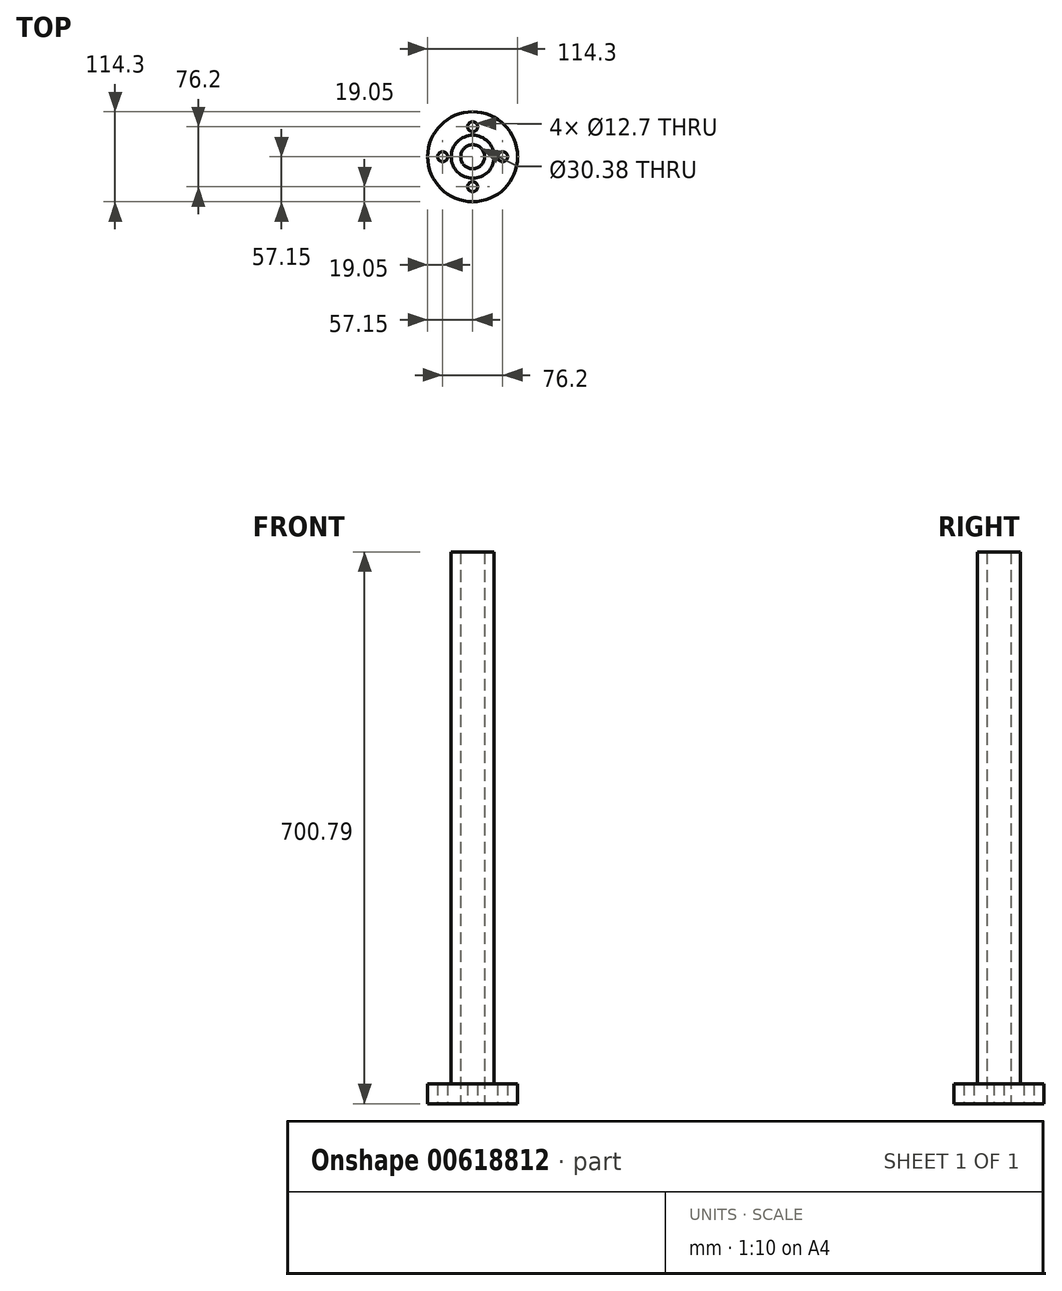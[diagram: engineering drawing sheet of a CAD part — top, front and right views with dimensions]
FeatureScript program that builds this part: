
annotation { "Feature Type Name" : "Feature", "Feature Type Description" : "" }
export const myFeature = defineFeature(function(context is Context, id is Id, definition is map)
    precondition{}
    {
        {
            var Q0;
            Q0=qCreatedBy(makeId("Top.planeOp"),FACE);
            var sketch = newSketch(context, id + "F0", { "sketchPlane" : qUnion([Q0])});
            skCircle(sketch, "E0", {"center": v(0, 0) * mm, "radius": 57.15 * mm});
            skCircle(sketch, "E1", {"center": v(0, 0) * mm, "radius": 27.32 * mm});
            skCircle(sketch, "E2", {"center": v(0, 0) * mm, "radius": 15.2 * mm});
            skCircle(sketch, "E3", {"center": v(0, 38.1) * mm, "radius": 6.35 * mm});
            skCircle(sketch, "E4.MirrorC", {"center": v(0, -38.1) * mm, "radius": 6.35 * mm});
            skCircle(sketch, "E5", {"center": v(38.1, 0) * mm, "radius": 6.35 * mm});
            skCircle(sketch, "E6", {"center": v(-38.1, 0) * mm, "radius": 6.35 * mm});
            skSolve(sketch);
        }
        {
            var Q0;
            Q0=qSketchRegion(id+"F0",true);
            extrude(context, id + "F1", {"entities" : qUnion([Q0]), "depth" : 25.4 * mm, "offsetDistance" : 25.4 * mm});
        }
        {
            var Q0;
            Q0=makeQuery(id+"F0.imprint","IMPRINT",FACE,{"disambiguationData":[TD([[makeQuery(id+"F0.imprint","IMPRINT",EDGE,{"derivedFrom":sQuery(id+"F0.wireOp",EDGE,"E1")}),1.0]])]});
            extrude(context, id + "F2", {"entities" : qUnion([Q0]), "operationType" : NewBodyOperationType.ADD, "depth" : 700.8 * mm, "offsetDistance" : 25.4 * mm});
        }
    });
